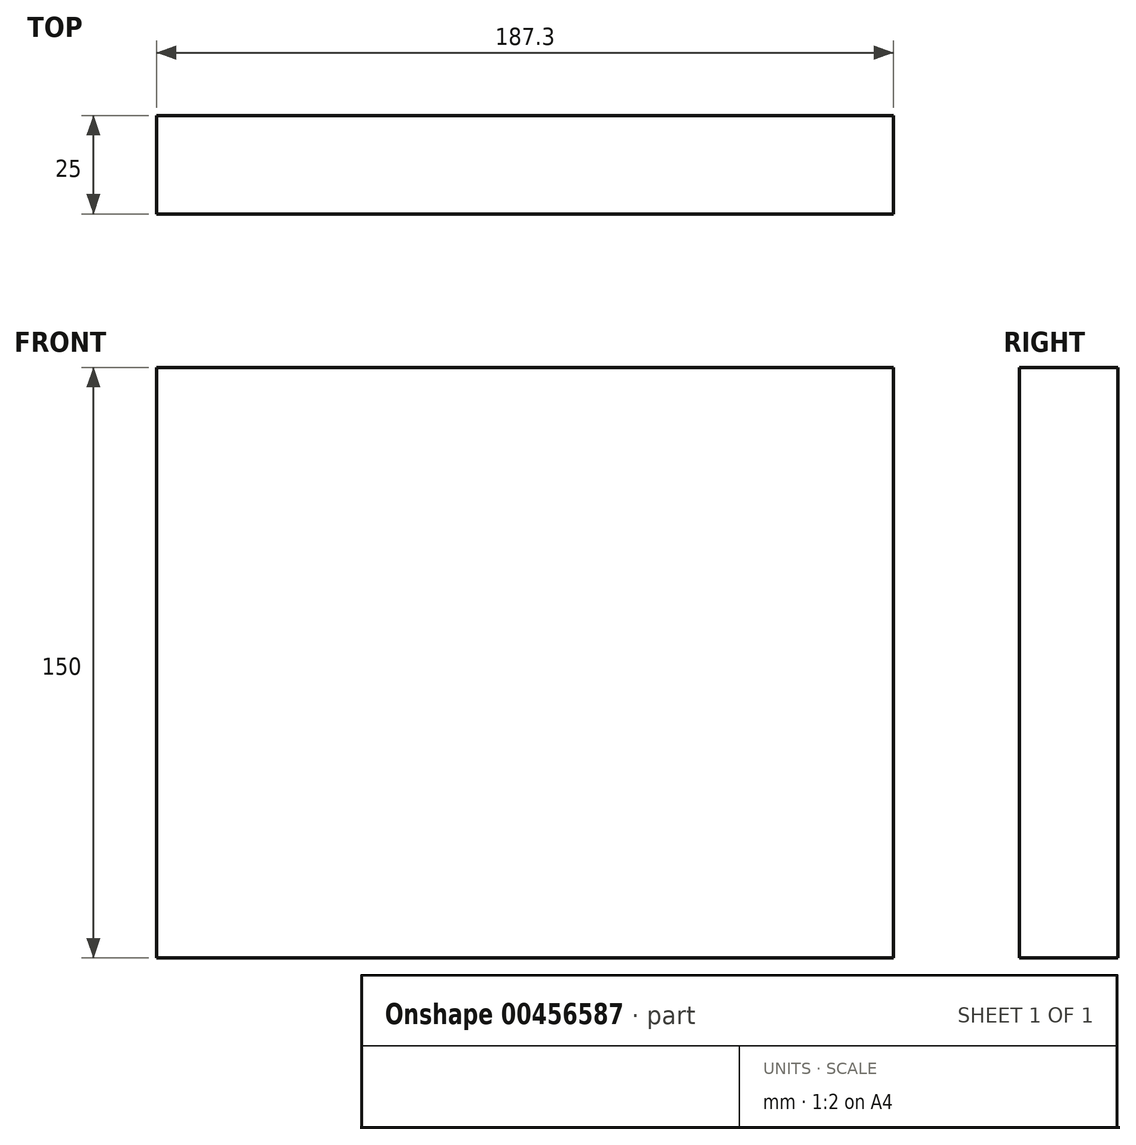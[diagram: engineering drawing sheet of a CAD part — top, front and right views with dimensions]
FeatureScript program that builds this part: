
annotation { "Feature Type Name" : "Feature", "Feature Type Description" : "" }
export const myFeature = defineFeature(function(context is Context, id is Id, definition is map)
    precondition{}
    {
        {
            var Q0;
            Q0=qCreatedBy(makeId("Front.planeOp"),FACE);
            var sketch = newSketch(context, id + "F0", { "sketchPlane" : qUnion([Q0])});
            skLineSegment(sketch, "E0.bottom", {"start": v(-101.63, 107.3) * mm, "end": v(85.67, 107.3) * mm});
            skLineSegment(sketch, "E0.top", {"start": v(-101.63, -42.7) * mm, "end": v(85.67, -42.7) * mm});
            skLineSegment(sketch, "E0.left", {"start": v(-101.63, 107.3) * mm, "end": v(-101.63, -42.7) * mm});
            skLineSegment(sketch, "E0.right", {"start": v(85.67, 107.3) * mm, "end": v(85.67, -42.7) * mm});
            skSolve(sketch);
        }
        {
            var Q0;
            Q0=qSketchRegion(id+"F0",true);
            extrude(context, id + "F1", {"entities" : qUnion([Q0]), "depth" : 25 * mm});
        }
    });
